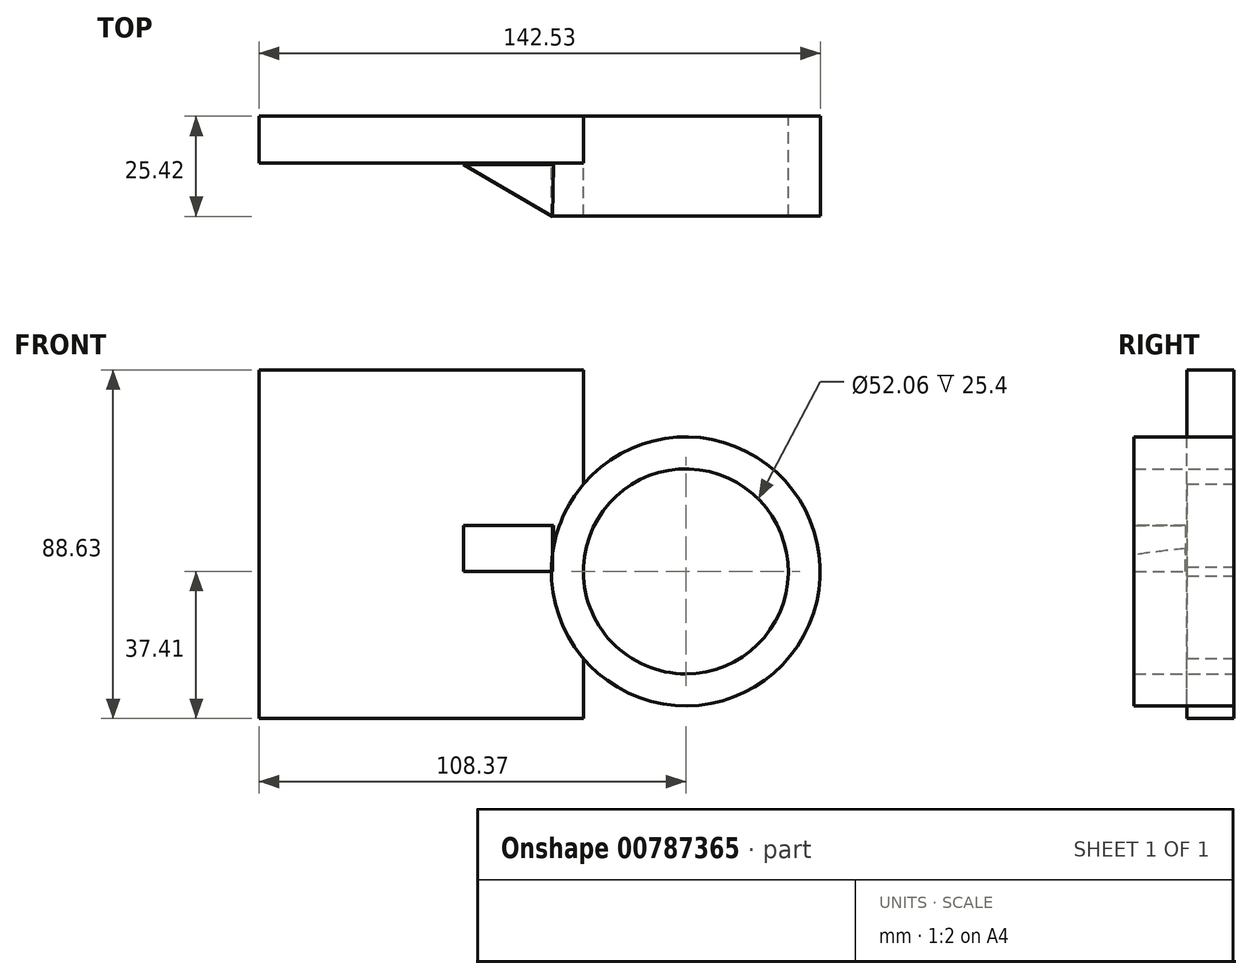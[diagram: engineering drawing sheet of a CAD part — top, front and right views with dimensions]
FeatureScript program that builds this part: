
annotation { "Feature Type Name" : "Feature", "Feature Type Description" : "" }
export const myFeature = defineFeature(function(context is Context, id is Id, definition is map)
    precondition{}
    {
        {
            var Q0;
            Q0=qCreatedBy(makeId("Front.planeOp"),FACE);
            var sketch = newSketch(context, id + "F0", { "sketchPlane" : qUnion([Q0])});
            skCircle(sketch, "E0", {"center": v(0, 0) * mm, "radius": 34.16 * mm});
            skCircle(sketch, "E1", {"center": v(0, 0) * mm, "radius": 26.03 * mm});
            skSolve(sketch);
        }
        {
            var Q0;
            Q0 = qSketchRegion(id + "F0", true);
            extrude(context, id + "F1", {"entities" : qUnion([Q0]), "depth" : 25.4 * mm, "offsetDistance" : 25.4 * mm});
        }
        {
            var Q0;
            Q0=qCreatedBy(makeId("Front.planeOp"),FACE);
            var sketch = newSketch(context, id + "F2", { "sketchPlane" : qUnion([Q0])});
            skLineSegment(sketch, "E2.bottom", {"start": v(-108.37, -37.41) * mm, "end": v(-26, -37.41) * mm});
            skLineSegment(sketch, "E2.top", {"start": v(-108.37, 51.22) * mm, "end": v(-26, 51.22) * mm});
            skLineSegment(sketch, "E2.left", {"start": v(-108.37, -37.41) * mm, "end": v(-108.37, 51.22) * mm});
            skLineSegment(sketch, "E2.right", {"start": v(-26, -37.41) * mm, "end": v(-26, 51.22) * mm});
            skSolve(sketch);
        }
        {
            var Q0;
            Q0 = qSketchRegion(id + "F2", true);
            extrude(context, id + "F3", {"entities" : qUnion([Q0]), "operationType" : NewBodyOperationType.ADD, "depth" : 11.94 * mm, "offsetDistance" : 25.4 * mm});
        }
        {
            var Q0;
            Q0=qCreatedBy(makeId("Top.planeOp"),FACE);
            var sketch = newSketch(context, id + "F4", { "sketchPlane" : qUnion([Q0])});
            skLineSegment(sketch, "E3", {"start": v(-33.9, -25.42) * mm, "end": v(-56.5, -12.32) * mm});
            skLineSegment(sketch, "E4", {"start": v(-56.5, -12.32) * mm, "end": v(-33.66, -12.32) * mm});
            skLineSegment(sketch, "E5", {"start": v(-33.66, -12.32) * mm, "end": v(-33.9, -25.42) * mm});
            skSolve(sketch);
        }
        {
            var Q0;
            Q0 = qSketchRegion(id + "F4", true);
            extrude(context, id + "F5", {"entities" : qUnion([Q0]), "operationType" : NewBodyOperationType.ADD, "depth" : 11.68 * mm, "offsetDistance" : 25.4 * mm});
        }
    });
